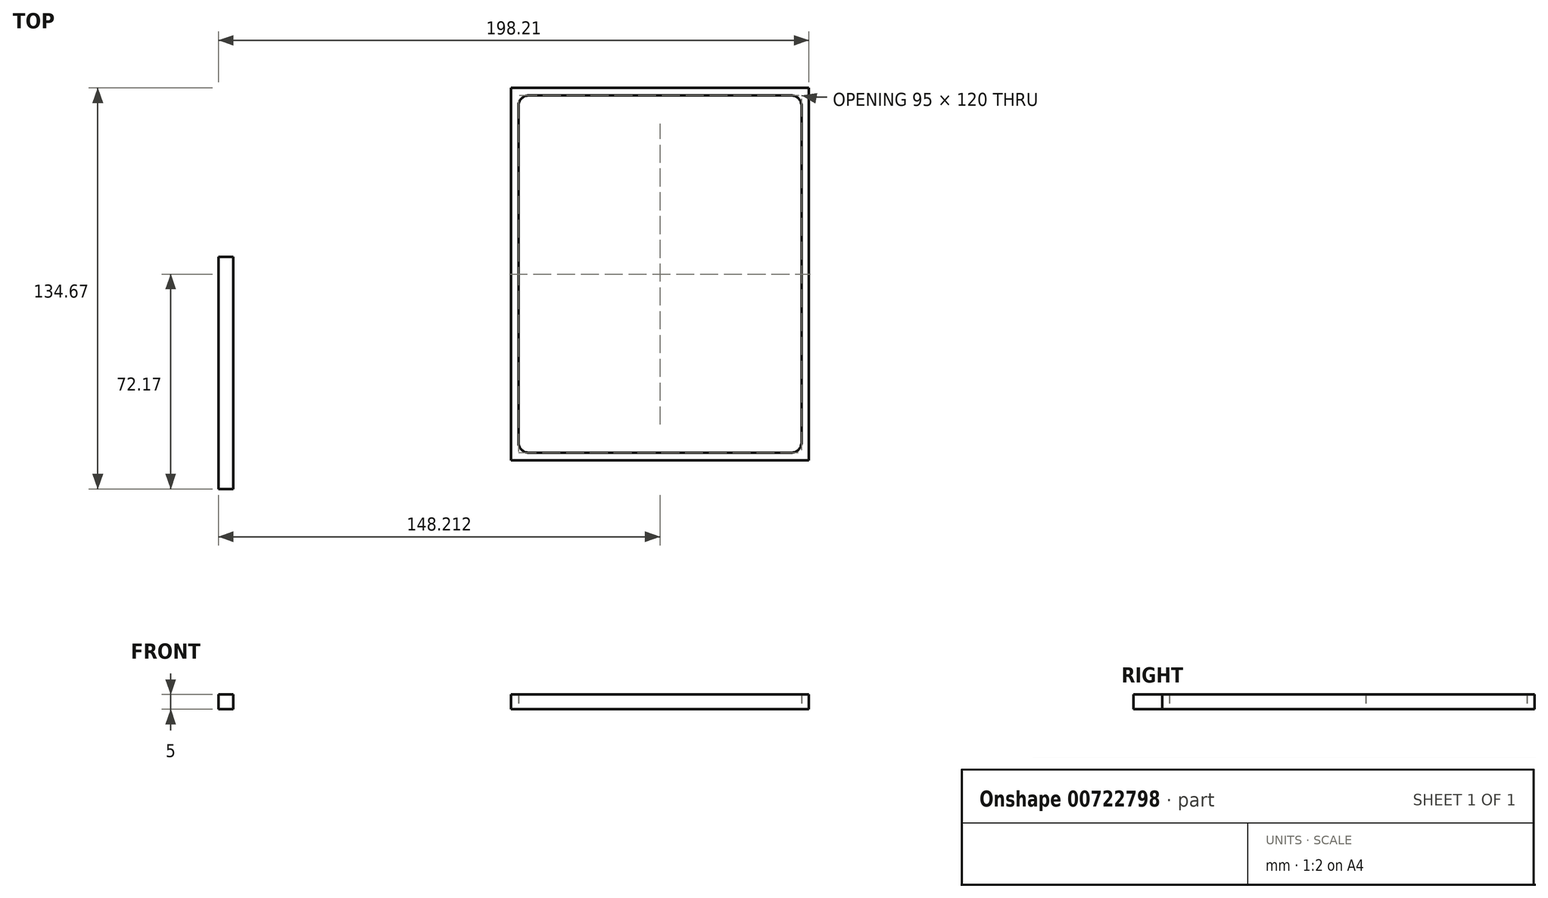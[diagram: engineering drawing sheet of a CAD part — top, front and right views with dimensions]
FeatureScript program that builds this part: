
annotation { "Feature Type Name" : "Feature", "Feature Type Description" : "" }
export const myFeature = defineFeature(function(context is Context, id is Id, definition is map)
    precondition{}
    {
        {
            var Q0;
            Q0=qCreatedBy(makeId("Top.planeOp"),FACE);
            var sketch = newSketch(context, id + "F0", { "sketchPlane" : qUnion([Q0])});
            skCircle(sketch, "E0", {"center": v(-29.27, 36.17) * mm, "radius": 8 * mm});
            skCircle(sketch, "E1", {"center": v(-29.27, 8.17) * mm, "radius": 8 * mm});
            skCircle(sketch, "E2", {"center": v(-29.27, -19.83) * mm, "radius": 8 * mm});
            skCircle(sketch, "E3", {"center": v(-29.27, -47.83) * mm, "radius": 8 * mm});
            skLineSegment(sketch, "E4.bottom", {"start": v(-47.27, 56.67) * mm, "end": v(52.73, 56.67) * mm});
            skLineSegment(sketch, "E4.top", {"start": v(-47.27, -68.33) * mm, "end": v(52.73, -68.33) * mm});
            skLineSegment(sketch, "E4.left", {"start": v(-47.27, 56.67) * mm, "end": v(-47.27, -68.33) * mm});
            skLineSegment(sketch, "E4.right", {"start": v(52.73, 56.67) * mm, "end": v(52.73, -68.33) * mm});
            skLineSegment(sketch, "E5", {"start": v(-11.8, -39.94) * mm, "end": v(-15.6, -39.94) * mm});
            skLineSegment(sketch, "E6", {"start": v(-15.6, -39.94) * mm, "end": v(-13.78, -36.83) * mm});
            skLineSegment(sketch, "E7", {"start": v(-13.78, -36.83) * mm, "end": v(-8.48, -36.83) * mm});
            skLineSegment(sketch, "E8", {"start": v(-8.48, -36.83) * mm, "end": v(-8.48, -58.83) * mm});
            skLineSegment(sketch, "E9", {"start": v(-11.8, -58.83) * mm, "end": v(-11.8, -39.94) * mm});
            skLineSegment(sketch, "E10", {"start": v(1.94, -39.94) * mm, "end": v(-1.87, -39.94) * mm});
            skLineSegment(sketch, "E11", {"start": v(-1.87, -39.94) * mm, "end": v(-0.04, -36.83) * mm});
            skLineSegment(sketch, "E12", {"start": v(-0.04, -36.83) * mm, "end": v(5.26, -36.83) * mm});
            skLineSegment(sketch, "E13", {"start": v(5.26, -36.83) * mm, "end": v(5.26, -58.83) * mm});
            skLineSegment(sketch, "E14", {"start": v(5.26, -58.83) * mm, "end": v(1.94, -58.83) * mm});
            skLineSegment(sketch, "E15", {"start": v(1.94, -58.83) * mm, "end": v(1.94, -39.94) * mm});
            skLineSegment(sketch, "E16", {"start": v(15.67, -39.94) * mm, "end": v(11.87, -39.94) * mm});
            skLineSegment(sketch, "E17", {"start": v(11.87, -39.94) * mm, "end": v(13.7, -36.83) * mm});
            skLineSegment(sketch, "E18", {"start": v(13.7, -36.83) * mm, "end": v(19, -36.83) * mm});
            skLineSegment(sketch, "E19", {"start": v(19, -36.83) * mm, "end": v(19, -58.83) * mm});
            skLineSegment(sketch, "E20", {"start": v(19, -58.83) * mm, "end": v(15.67, -58.83) * mm});
            skLineSegment(sketch, "E21", {"start": v(15.67, -58.83) * mm, "end": v(15.67, -39.94) * mm});
            skFitSpline(sketch, "E22", {"points": [v(28.68, -47.39) * mm, v(27.07, -46.25) * mm, v(26.26, -44.7) * mm, v(26.26, -42.73) * mm]});
            skFitSpline(sketch, "E23", {"points": [v(26.26, -42.73) * mm, v(26.26, -40.94) * mm, v(26.87, -39.45) * mm, v(28.1, -38.25) * mm]});
            skFitSpline(sketch, "E24", {"points": [v(28.1, -38.25) * mm, v(29.33, -37.06) * mm, v(30.87, -36.46) * mm, v(32.7, -36.46) * mm]});
            skFitSpline(sketch, "E25", {"points": [v(32.7, -36.46) * mm, v(34.52, -36.46) * mm, v(36.04, -37.06) * mm, v(37.26, -38.25) * mm]});
            skFitSpline(sketch, "E26", {"points": [v(37.26, -38.25) * mm, v(38.47, -39.44) * mm, v(39.08, -40.94) * mm, v(39.08, -42.74) * mm]});
            skFitSpline(sketch, "E27", {"points": [v(39.08, -42.74) * mm, v(39.08, -44.63) * mm, v(38.28, -46.18) * mm, v(36.67, -47.37) * mm]});
            skFitSpline(sketch, "E28", {"points": [v(36.67, -47.37) * mm, v(37.56, -47.85) * mm, v(38.25, -48.54) * mm, v(38.75, -49.45) * mm]});
            skFitSpline(sketch, "E29", {"points": [v(38.75, -49.45) * mm, v(39.27, -50.37) * mm, v(39.52, -51.4) * mm, v(39.52, -52.53) * mm]});
            skFitSpline(sketch, "E30", {"points": [v(39.52, -52.53) * mm, v(39.52, -54.48) * mm, v(38.89, -56.07) * mm, v(37.61, -57.32) * mm]});
            skFitSpline(sketch, "E31", {"points": [v(37.61, -57.32) * mm, v(36.34, -58.56) * mm, v(34.71, -59.19) * mm, v(32.73, -59.19) * mm]});
            skFitSpline(sketch, "E32", {"points": [v(32.73, -59.19) * mm, v(30.7, -59.19) * mm, v(29.02, -58.56) * mm, v(27.7, -57.3) * mm]});
            skFitSpline(sketch, "E33", {"points": [v(27.7, -57.3) * mm, v(26.37, -56.05) * mm, v(25.7, -54.47) * mm, v(25.7, -52.57) * mm]});
            skFitSpline(sketch, "E34", {"points": [v(25.7, -52.57) * mm, v(25.7, -50.1) * mm, v(26.7, -48.38) * mm, v(28.68, -47.39) * mm]});
            skFitSpline(sketch, "E35", {"points": [v(29.38, -42.71) * mm, v(29.38, -43.65) * mm, v(29.7, -44.44) * mm, v(30.33, -45.08) * mm]});
            skFitSpline(sketch, "E36", {"points": [v(30.33, -45.08) * mm, v(30.98, -45.73) * mm, v(31.76, -46.05) * mm, v(32.67, -46.05) * mm]});
            skFitSpline(sketch, "E37", {"points": [v(32.67, -46.05) * mm, v(33.57, -46.05) * mm, v(34.35, -45.73) * mm, v(35, -45.08) * mm]});
            skFitSpline(sketch, "E38", {"points": [v(35, -45.08) * mm, v(35.64, -44.43) * mm, v(35.96, -43.66) * mm, v(35.96, -42.76) * mm]});
            skFitSpline(sketch, "E39", {"points": [v(35.96, -42.76) * mm, v(35.96, -41.85) * mm, v(35.64, -41.08) * mm, v(35, -40.43) * mm]});
            skFitSpline(sketch, "E40", {"points": [v(35, -40.43) * mm, v(34.35, -39.79) * mm, v(33.57, -39.47) * mm, v(32.67, -39.47) * mm]});
            skFitSpline(sketch, "E41", {"points": [v(32.67, -39.47) * mm, v(31.77, -39.47) * mm, v(31, -39.79) * mm, v(30.35, -40.43) * mm]});
            skFitSpline(sketch, "E42", {"points": [v(30.35, -40.43) * mm, v(29.7, -41.08) * mm, v(29.38, -41.84) * mm, v(29.38, -42.71) * mm]});
            skFitSpline(sketch, "E43", {"points": [v(28.97, -52.46) * mm, v(28.97, -53.48) * mm, v(29.32, -54.35) * mm, v(30.02, -55.08) * mm]});
            skFitSpline(sketch, "E44", {"points": [v(30.02, -55.08) * mm, v(30.73, -55.8) * mm, v(31.6, -56.17) * mm, v(32.61, -56.17) * mm]});
            skFitSpline(sketch, "E45", {"points": [v(32.61, -56.17) * mm, v(33.62, -56.17) * mm, v(34.48, -55.8) * mm, v(35.2, -55.1) * mm]});
            skFitSpline(sketch, "E46", {"points": [v(35.2, -55.1) * mm, v(35.9, -54.37) * mm, v(36.26, -53.51) * mm, v(36.26, -52.5) * mm]});
            skFitSpline(sketch, "E47", {"points": [v(36.26, -52.5) * mm, v(36.26, -51.49) * mm, v(35.9, -50.62) * mm, v(35.2, -49.91) * mm]});
            skFitSpline(sketch, "E48", {"points": [v(35.2, -49.91) * mm, v(34.48, -49.2) * mm, v(33.62, -48.84) * mm, v(32.61, -48.84) * mm]});
            skFitSpline(sketch, "E49", {"points": [v(32.61, -48.84) * mm, v(31.62, -48.84) * mm, v(30.76, -49.2) * mm, v(30.03, -49.91) * mm]});
            skFitSpline(sketch, "E50", {"points": [v(30.03, -49.91) * mm, v(29.32, -50.62) * mm, v(28.97, -51.47) * mm, v(28.97, -52.46) * mm]});
            skLineSegment(sketch, "E51", {"start": v(-11.8, -11.94) * mm, "end": v(-15.6, -11.94) * mm});
            skLineSegment(sketch, "E52", {"start": v(-15.6, -11.94) * mm, "end": v(-13.78, -8.83) * mm});
            skLineSegment(sketch, "E53", {"start": v(-13.78, -8.83) * mm, "end": v(-8.48, -8.83) * mm});
            skLineSegment(sketch, "E54", {"start": v(-8.48, -8.83) * mm, "end": v(-8.48, -30.83) * mm});
            skLineSegment(sketch, "E55", {"start": v(-8.48, -30.83) * mm, "end": v(-11.8, -30.83) * mm});
            skLineSegment(sketch, "E56", {"start": v(-11.8, -30.83) * mm, "end": v(-11.8, -11.94) * mm});
            skLineSegment(sketch, "E57", {"start": v(1.94, -11.94) * mm, "end": v(-1.87, -11.94) * mm});
            skLineSegment(sketch, "E58", {"start": v(-1.87, -11.94) * mm, "end": v(-0.04, -8.83) * mm});
            skLineSegment(sketch, "E59", {"start": v(-0.04, -8.83) * mm, "end": v(5.26, -8.83) * mm});
            skLineSegment(sketch, "E60", {"start": v(5.26, -8.83) * mm, "end": v(5.26, -30.83) * mm});
            skLineSegment(sketch, "E61", {"start": v(5.26, -30.83) * mm, "end": v(1.94, -30.83) * mm});
            skLineSegment(sketch, "E62", {"start": v(1.94, -30.83) * mm, "end": v(1.94, -11.94) * mm});
            skLineSegment(sketch, "E63", {"start": v(17.07, -27.7) * mm, "end": v(25.26, -27.7) * mm});
            skLineSegment(sketch, "E64", {"start": v(25.26, -27.7) * mm, "end": v(25.26, -30.83) * mm});
            skLineSegment(sketch, "E65", {"start": v(25.26, -30.83) * mm, "end": v(10.49, -30.83) * mm});
            skLineSegment(sketch, "E66", {"start": v(10.49, -30.83) * mm, "end": v(18.12, -21.58) * mm});
            skFitSpline(sketch, "E67", {"points": [v(18.12, -21.58) * mm, v(18.87, -20.66) * mm, v(19.5, -19.86) * mm, v(20, -19.19) * mm]});
            skFitSpline(sketch, "E68", {"points": [v(20, -19.19) * mm, v(20.52, -18.51) * mm, v(20.9, -17.95) * mm, v(21.17, -17.5) * mm]});
            skFitSpline(sketch, "E69", {"points": [v(21.17, -17.5) * mm, v(21.71, -16.6) * mm, v(21.99, -15.8) * mm, v(21.99, -15.08) * mm]});
            skFitSpline(sketch, "E70", {"points": [v(21.99, -15.08) * mm, v(21.99, -14.06) * mm, v(21.62, -13.2) * mm, v(20.9, -12.5) * mm]});
            skFitSpline(sketch, "E71", {"points": [v(20.9, -12.5) * mm, v(20.18, -11.81) * mm, v(19.29, -11.47) * mm, v(18.22, -11.47) * mm]});
            skFitSpline(sketch, "E72", {"points": [v(18.22, -11.47) * mm, v(16, -11.47) * mm, v(14.73, -12.78) * mm, v(14.4, -15.41) * mm]});
            skLineSegment(sketch, "E73", {"start": v(14.4, -15.41) * mm, "end": v(11.1, -15.41) * mm});
            skFitSpline(sketch, "E74", {"points": [v(11.1, -15.41) * mm, v(11.63, -10.78) * mm, v(13.97, -8.46) * mm, v(18.12, -8.46) * mm]});
            skFitSpline(sketch, "E75", {"points": [v(18.12, -8.46) * mm, v(20.13, -8.46) * mm, v(21.8, -9.1) * mm, v(23.17, -10.37) * mm]});
            skFitSpline(sketch, "E76", {"points": [v(23.17, -10.37) * mm, v(24.54, -11.64) * mm, v(25.22, -13.22) * mm, v(25.22, -15.1) * mm]});
            skFitSpline(sketch, "E77", {"points": [v(25.22, -15.1) * mm, v(25.22, -16.3) * mm, v(24.9, -17.47) * mm, v(24.26, -18.62) * mm]});
            skFitSpline(sketch, "E78", {"points": [v(24.26, -18.62) * mm, v(23.94, -19.22) * mm, v(23.47, -19.93) * mm, v(22.84, -20.76) * mm]});
            skFitSpline(sketch, "E79", {"points": [v(22.84, -20.76) * mm, v(22.22, -21.57) * mm, v(21.44, -22.54) * mm, v(20.49, -23.66) * mm]});
            skLineSegment(sketch, "E80", {"start": v(20.49, -23.66) * mm, "end": v(17.07, -27.7) * mm});
            skFitSpline(sketch, "E81", {"points": [v(29, -19.69) * mm, v(29, -16.18) * mm, v(29.83, -13.38) * mm, v(31.46, -11.3) * mm]});
            skFitSpline(sketch, "E82", {"points": [v(31.46, -11.3) * mm, v(32.92, -9.4) * mm, v(34.7, -8.46) * mm, v(36.78, -8.46) * mm]});
            skFitSpline(sketch, "E83", {"points": [v(36.78, -8.46) * mm, v(38.86, -8.46) * mm, v(40.63, -9.4) * mm, v(42.09, -11.3) * mm]});
            skFitSpline(sketch, "E84", {"points": [v(42.09, -11.3) * mm, v(43.72, -13.38) * mm, v(44.54, -16.23) * mm, v(44.54, -19.83) * mm]});
            skFitSpline(sketch, "E85", {"points": [v(44.54, -19.83) * mm, v(44.54, -23.42) * mm, v(43.72, -26.26) * mm, v(42.09, -28.35) * mm]});
            skFitSpline(sketch, "E86", {"points": [v(42.09, -28.35) * mm, v(40.63, -30.24) * mm, v(38.86, -31.19) * mm, v(36.79, -31.19) * mm]});
            skFitSpline(sketch, "E87", {"points": [v(36.79, -31.19) * mm, v(34.72, -31.19) * mm, v(32.94, -30.24) * mm, v(31.46, -28.35) * mm]});
            skFitSpline(sketch, "E88", {"points": [v(31.46, -28.35) * mm, v(29.83, -26.26) * mm, v(29, -23.37) * mm, v(29, -19.69) * mm]});
            skFitSpline(sketch, "E89", {"points": [v(32.27, -19.7) * mm, v(32.27, -22.14) * mm, v(32.7, -24.17) * mm, v(33.54, -25.79) * mm]});
            skFitSpline(sketch, "E90", {"points": [v(33.54, -25.79) * mm, v(34.39, -27.37) * mm, v(35.46, -28.17) * mm, v(36.78, -28.17) * mm]});
            skFitSpline(sketch, "E91", {"points": [v(36.78, -28.17) * mm, v(38.08, -28.17) * mm, v(39.15, -27.37) * mm, v(40, -25.79) * mm]});
            skFitSpline(sketch, "E92", {"points": [v(40, -25.79) * mm, v(40.86, -24.2) * mm, v(41.3, -22.22) * mm, v(41.3, -19.82) * mm]});
            skFitSpline(sketch, "E93", {"points": [v(41.3, -19.82) * mm, v(41.3, -17.41) * mm, v(40.86, -15.42) * mm, v(40, -13.83) * mm]});
            skFitSpline(sketch, "E94", {"points": [v(40, -13.83) * mm, v(39.15, -12.25) * mm, v(38.08, -11.47) * mm, v(36.78, -11.47) * mm]});
            skFitSpline(sketch, "E95", {"points": [v(36.78, -11.47) * mm, v(35.48, -11.47) * mm, v(34.4, -12.25) * mm, v(33.55, -13.83) * mm]});
            skFitSpline(sketch, "E96", {"points": [v(33.55, -13.83) * mm, v(32.7, -15.4) * mm, v(32.27, -17.36) * mm, v(32.27, -19.7) * mm]});
            skLineSegment(sketch, "E97", {"start": v(-11.86, 16.06) * mm, "end": v(-15.66, 16.06) * mm});
            skLineSegment(sketch, "E98", {"start": v(-15.66, 16.06) * mm, "end": v(-13.84, 19.17) * mm});
            skLineSegment(sketch, "E99", {"start": v(-13.84, 19.17) * mm, "end": v(-8.54, 19.17) * mm});
            skLineSegment(sketch, "E100", {"start": v(-8.54, 19.17) * mm, "end": v(-8.54, -2.83) * mm});
            skLineSegment(sketch, "E101", {"start": v(-8.54, -2.83) * mm, "end": v(-11.86, -2.83) * mm});
            skLineSegment(sketch, "E102", {"start": v(-11.86, -2.83) * mm, "end": v(-11.86, 16.06) * mm});
            skLineSegment(sketch, "E103", {"start": v(1.88, 16.06) * mm, "end": v(-1.93, 16.06) * mm});
            skLineSegment(sketch, "E104", {"start": v(-1.93, 16.06) * mm, "end": v(-0.1, 19.17) * mm});
            skLineSegment(sketch, "E105", {"start": v(-0.1, 19.17) * mm, "end": v(5.2, 19.17) * mm});
            skLineSegment(sketch, "E106", {"start": v(5.2, 19.17) * mm, "end": v(5.2, -2.83) * mm});
            skLineSegment(sketch, "E107", {"start": v(5.2, -2.83) * mm, "end": v(1.88, -2.83) * mm});
            skLineSegment(sketch, "E108", {"start": v(1.88, -2.83) * mm, "end": v(1.88, 16.06) * mm});
            skLineSegment(sketch, "E109", {"start": v(17, 0.3) * mm, "end": v(25.2, 0.3) * mm});
            skLineSegment(sketch, "E110", {"start": v(25.2, 0.3) * mm, "end": v(25.2, -2.83) * mm});
            skLineSegment(sketch, "E111", {"start": v(25.2, -2.83) * mm, "end": v(10.42, -2.83) * mm});
            skLineSegment(sketch, "E112", {"start": v(10.42, -2.83) * mm, "end": v(18.06, 6.42) * mm});
            skFitSpline(sketch, "E113", {"points": [v(18.06, 6.42) * mm, v(18.81, 7.34) * mm, v(19.44, 8.14) * mm, v(19.94, 8.81) * mm]});
            skFitSpline(sketch, "E114", {"points": [v(19.94, 8.81) * mm, v(20.46, 9.49) * mm, v(20.85, 10.05) * mm, v(21.11, 10.5) * mm]});
            skFitSpline(sketch, "E115", {"points": [v(21.11, 10.5) * mm, v(21.65, 11.4) * mm, v(21.92, 12.2) * mm, v(21.92, 12.92) * mm]});
            skFitSpline(sketch, "E116", {"points": [v(21.92, 12.92) * mm, v(21.92, 13.94) * mm, v(21.56, 14.8) * mm, v(20.84, 15.5) * mm]});
            skFitSpline(sketch, "E117", {"points": [v(20.84, 15.5) * mm, v(20.12, 16.19) * mm, v(19.23, 16.53) * mm, v(18.16, 16.53) * mm]});
            skFitSpline(sketch, "E118", {"points": [v(18.16, 16.53) * mm, v(15.94, 16.53) * mm, v(14.67, 15.22) * mm, v(14.34, 12.59) * mm]});
            skLineSegment(sketch, "E119", {"start": v(14.34, 12.59) * mm, "end": v(11.04, 12.59) * mm});
            skFitSpline(sketch, "E120", {"points": [v(11.04, 12.59) * mm, v(11.57, 17.22) * mm, v(13.91, 19.54) * mm, v(18.06, 19.54) * mm]});
            skFitSpline(sketch, "E121", {"points": [v(18.06, 19.54) * mm, v(20.07, 19.54) * mm, v(21.75, 18.9) * mm, v(23.1, 17.63) * mm]});
            skFitSpline(sketch, "E122", {"points": [v(23.1, 17.63) * mm, v(24.47, 16.36) * mm, v(25.16, 14.78) * mm, v(25.16, 12.9) * mm]});
            skFitSpline(sketch, "E123", {"points": [v(25.16, 12.9) * mm, v(25.16, 11.7) * mm, v(24.84, 10.53) * mm, v(24.2, 9.38) * mm]});
            skFitSpline(sketch, "E124", {"points": [v(24.2, 9.38) * mm, v(23.88, 8.78) * mm, v(23.4, 8.07) * mm, v(22.78, 7.24) * mm]});
            skFitSpline(sketch, "E125", {"points": [v(22.78, 7.24) * mm, v(22.16, 6.43) * mm, v(21.38, 5.46) * mm, v(20.43, 4.34) * mm]});
            skLineSegment(sketch, "E126", {"start": v(20.43, 4.34) * mm, "end": v(17, 0.3) * mm});
            skLineSegment(sketch, "E127", {"start": v(35.02, 0.3) * mm, "end": v(43.21, 0.3) * mm});
            skLineSegment(sketch, "E128", {"start": v(43.21, 0.3) * mm, "end": v(43.21, -2.83) * mm});
            skLineSegment(sketch, "E129", {"start": v(43.21, -2.83) * mm, "end": v(28.44, -2.83) * mm});
            skLineSegment(sketch, "E130", {"start": v(28.44, -2.83) * mm, "end": v(36.07, 6.42) * mm});
            skFitSpline(sketch, "E131", {"points": [v(36.07, 6.42) * mm, v(36.82, 7.34) * mm, v(37.45, 8.14) * mm, v(37.95, 8.81) * mm]});
            skFitSpline(sketch, "E132", {"points": [v(37.95, 8.81) * mm, v(38.47, 9.49) * mm, v(38.86, 10.05) * mm, v(39.12, 10.5) * mm]});
            skFitSpline(sketch, "E133", {"points": [v(39.12, 10.5) * mm, v(39.66, 11.4) * mm, v(39.93, 12.2) * mm, v(39.93, 12.92) * mm]});
            skFitSpline(sketch, "E134", {"points": [v(39.93, 12.92) * mm, v(39.93, 13.94) * mm, v(39.57, 14.8) * mm, v(38.85, 15.5) * mm]});
            skFitSpline(sketch, "E135", {"points": [v(38.85, 15.5) * mm, v(38.13, 16.19) * mm, v(37.24, 16.53) * mm, v(36.17, 16.53) * mm]});
            skFitSpline(sketch, "E136", {"points": [v(36.17, 16.53) * mm, v(33.95, 16.53) * mm, v(32.68, 15.22) * mm, v(32.35, 12.59) * mm]});
            skLineSegment(sketch, "E137", {"start": v(32.35, 12.59) * mm, "end": v(29.05, 12.59) * mm});
            skFitSpline(sketch, "E138", {"points": [v(29.05, 12.59) * mm, v(29.58, 17.22) * mm, v(31.92, 19.54) * mm, v(36.07, 19.54) * mm]});
            skFitSpline(sketch, "E139", {"points": [v(36.07, 19.54) * mm, v(38.08, 19.54) * mm, v(39.76, 18.9) * mm, v(41.12, 17.63) * mm]});
            skFitSpline(sketch, "E140", {"points": [v(41.12, 17.63) * mm, v(42.48, 16.36) * mm, v(43.17, 14.78) * mm, v(43.17, 12.9) * mm]});
            skFitSpline(sketch, "E141", {"points": [v(43.17, 12.9) * mm, v(43.17, 11.7) * mm, v(42.85, 10.53) * mm, v(42.21, 9.38) * mm]});
            skFitSpline(sketch, "E142", {"points": [v(42.21, 9.38) * mm, v(41.9, 8.78) * mm, v(41.42, 8.07) * mm, v(40.79, 7.24) * mm]});
            skFitSpline(sketch, "E143", {"points": [v(40.79, 7.24) * mm, v(40.17, 6.43) * mm, v(39.39, 5.46) * mm, v(38.44, 4.34) * mm]});
            skLineSegment(sketch, "E144", {"start": v(38.44, 4.34) * mm, "end": v(35.02, 0.3) * mm});
            skLineSegment(sketch, "E145", {"start": v(-11.74, 44.06) * mm, "end": v(-15.55, 44.06) * mm});
            skLineSegment(sketch, "E146", {"start": v(-15.55, 44.06) * mm, "end": v(-13.72, 47.17) * mm});
            skLineSegment(sketch, "E147", {"start": v(-13.72, 47.17) * mm, "end": v(-8.42, 47.17) * mm});
            skLineSegment(sketch, "E148", {"start": v(-8.42, 47.17) * mm, "end": v(-8.42, 25.17) * mm});
            skLineSegment(sketch, "E149", {"start": v(-8.42, 25.17) * mm, "end": v(-11.74, 25.17) * mm});
            skLineSegment(sketch, "E150", {"start": v(-11.74, 25.17) * mm, "end": v(-11.74, 44.06) * mm});
            skLineSegment(sketch, "E151", {"start": v(2, 44.06) * mm, "end": v(-1.8, 44.06) * mm});
            skLineSegment(sketch, "E152", {"start": v(-1.8, 44.06) * mm, "end": v(0.01, 47.17) * mm});
            skLineSegment(sketch, "E153", {"start": v(0.01, 47.17) * mm, "end": v(5.31, 47.17) * mm});
            skLineSegment(sketch, "E154", {"start": v(5.31, 47.17) * mm, "end": v(5.31, 25.17) * mm});
            skLineSegment(sketch, "E155", {"start": v(5.31, 25.17) * mm, "end": v(2, 25.17) * mm});
            skLineSegment(sketch, "E156", {"start": v(2, 25.17) * mm, "end": v(2, 44.06) * mm});
            skLineSegment(sketch, "E157", {"start": v(17.13, 28.3) * mm, "end": v(25.32, 28.3) * mm});
            skLineSegment(sketch, "E158", {"start": v(25.32, 28.3) * mm, "end": v(25.32, 25.17) * mm});
            skLineSegment(sketch, "E159", {"start": v(25.32, 25.17) * mm, "end": v(10.54, 25.17) * mm});
            skLineSegment(sketch, "E160", {"start": v(10.54, 25.17) * mm, "end": v(18.18, 34.42) * mm});
            skFitSpline(sketch, "E161", {"points": [v(18.18, 34.42) * mm, v(18.93, 35.34) * mm, v(19.56, 36.14) * mm, v(20.06, 36.81) * mm]});
            skFitSpline(sketch, "E162", {"points": [v(20.06, 36.81) * mm, v(20.58, 37.49) * mm, v(20.96, 38.05) * mm, v(21.23, 38.5) * mm]});
            skFitSpline(sketch, "E163", {"points": [v(21.23, 38.5) * mm, v(21.77, 39.4) * mm, v(22.04, 40.2) * mm, v(22.04, 40.92) * mm]});
            skFitSpline(sketch, "E164", {"points": [v(22.04, 40.92) * mm, v(22.04, 41.94) * mm, v(21.68, 42.8) * mm, v(20.96, 43.5) * mm]});
            skFitSpline(sketch, "E165", {"points": [v(20.96, 43.5) * mm, v(20.24, 44.19) * mm, v(19.35, 44.53) * mm, v(18.28, 44.53) * mm]});
            skFitSpline(sketch, "E166", {"points": [v(18.28, 44.53) * mm, v(16.06, 44.53) * mm, v(14.79, 43.22) * mm, v(14.46, 40.59) * mm]});
            skLineSegment(sketch, "E167", {"start": v(14.46, 40.59) * mm, "end": v(11.16, 40.59) * mm});
            skFitSpline(sketch, "E168", {"points": [v(11.16, 40.59) * mm, v(11.69, 45.22) * mm, v(14.03, 47.54) * mm, v(18.18, 47.54) * mm]});
            skFitSpline(sketch, "E169", {"points": [v(18.18, 47.54) * mm, v(20.19, 47.54) * mm, v(21.87, 46.9) * mm, v(23.23, 45.63) * mm]});
            skFitSpline(sketch, "E170", {"points": [v(23.23, 45.63) * mm, v(24.6, 44.36) * mm, v(25.28, 42.78) * mm, v(25.28, 40.9) * mm]});
            skFitSpline(sketch, "E171", {"points": [v(25.28, 40.9) * mm, v(25.28, 39.7) * mm, v(24.96, 38.53) * mm, v(24.32, 37.38) * mm]});
            skFitSpline(sketch, "E172", {"points": [v(24.32, 37.38) * mm, v(24, 36.78) * mm, v(23.52, 36.07) * mm, v(22.9, 35.24) * mm]});
            skFitSpline(sketch, "E173", {"points": [v(22.9, 35.24) * mm, v(22.28, 34.43) * mm, v(21.5, 33.46) * mm, v(20.55, 32.34) * mm]});
            skLineSegment(sketch, "E174", {"start": v(20.55, 32.34) * mm, "end": v(17.13, 28.3) * mm});
            skLineSegment(sketch, "E175", {"start": v(42.05, 31.31) * mm, "end": v(44.38, 31.31) * mm});
            skLineSegment(sketch, "E176", {"start": v(44.38, 31.31) * mm, "end": v(44.38, 28.3) * mm});
            skLineSegment(sketch, "E177", {"start": v(44.38, 28.3) * mm, "end": v(42.05, 28.3) * mm});
            skLineSegment(sketch, "E178", {"start": v(42.05, 28.3) * mm, "end": v(42.05, 25.17) * mm});
            skLineSegment(sketch, "E179", {"start": v(42.05, 25.17) * mm, "end": v(38.73, 25.17) * mm});
            skLineSegment(sketch, "E180", {"start": v(38.73, 25.17) * mm, "end": v(38.73, 28.3) * mm});
            skLineSegment(sketch, "E181", {"start": v(38.73, 28.3) * mm, "end": v(27.93, 28.3) * mm});
            skLineSegment(sketch, "E182", {"start": v(27.93, 28.3) * mm, "end": v(42.05, 48.8) * mm});
            skLineSegment(sketch, "E183", {"start": v(42.05, 48.8) * mm, "end": v(42.05, 43.5) * mm});
            skLineSegment(sketch, "E184", {"start": v(38.73, 31.31) * mm, "end": v(38.73, 35) * mm});
            skLineSegment(sketch, "E185", {"start": v(38.73, 38.68) * mm, "end": v(33.66, 31.31) * mm});
            skLineSegment(sketch, "E186", {"start": v(33.66, 31.31) * mm, "end": v(38.73, 31.31) * mm});
            skCircle(sketch, "E187", {"center": v(-41.27, 50.67) * mm, "radius": 1.75 * mm});
            skCircle(sketch, "E188", {"center": v(46.73, 50.67) * mm, "radius": 1.75 * mm});
            skCircle(sketch, "E189", {"center": v(-41.27, -62.33) * mm, "radius": 1.75 * mm});
            skCircle(sketch, "E190", {"center": v(46.73, -62.33) * mm, "radius": 1.75 * mm});
            skLineSegment(sketch, "E191", {"start": v(33.66, 31.31) * mm, "end": v(42.05, 43.5) * mm});
            skLineSegment(sketch, "E192", {"start": v(38.73, 35) * mm, "end": v(42.05, 35) * mm});
            skLineSegment(sketch, "E193.trimOffspring", {"start": v(42.05, 35) * mm, "end": v(42.05, 31.31) * mm});
            skPoint(sketch, "E194.orphan", {"position": v(38.73, 38.68) * mm});
            skLineSegment(sketch, "E195.left", {"start": v(36.03, -8.5) * mm, "end": v(36.03, -11.56) * mm});
            skLineSegment(sketch, "E195.right", {"start": v(37.54, -8.5) * mm, "end": v(37.54, -11.56) * mm});
            skLineSegment(sketch, "E196.trimOffspring", {"start": v(36.03, -28.07) * mm, "end": v(36.03, -31.14) * mm});
            skLineSegment(sketch, "E197.trimOffspring", {"start": v(37.54, -28.07) * mm, "end": v(37.54, -31.14) * mm});
            skLineSegment(sketch, "E198.left", {"start": v(31.91, -36.5) * mm, "end": v(31.91, -39.55) * mm});
            skLineSegment(sketch, "E198.right", {"start": v(33.43, -36.5) * mm, "end": v(33.43, -39.55) * mm});
            skLineSegment(sketch, "E199.trimOffspring", {"start": v(33.43, -56.08) * mm, "end": v(33.43, -59.16) * mm});
            skLineSegment(sketch, "E200.trimOffspring", {"start": v(31.91, -56.1) * mm, "end": v(31.91, -59.15) * mm});
            skLineSegment(sketch, "E201.trimOffspring", {"start": v(33.43, -45.97) * mm, "end": v(33.43, -48.93) * mm});
            skLineSegment(sketch, "E202.trimOffspring", {"start": v(31.91, -45.97) * mm, "end": v(31.91, -48.9) * mm});
            skLineSegment(sketch, "E203", {"start": v(-11.8, -58.83) * mm, "end": v(-8.48, -58.83) * mm});
            skCircle(sketch, "E204", {"center": v(-41.27, 50.67) * mm, "radius": 3.5 * mm});
            skCircle(sketch, "E205", {"center": v(46.73, 50.67) * mm, "radius": 3.5 * mm});
            skCircle(sketch, "E206", {"center": v(-41.27, -62.33) * mm, "radius": 3.5 * mm});
            skCircle(sketch, "E207", {"center": v(46.73, -62.33) * mm, "radius": 3.5 * mm});
            skLineSegment(sketch, "E208", {"start": v(50.23, -62.33) * mm, "end": v(50.23, 50.67) * mm});
            skLineSegment(sketch, "E209", {"start": v(-44.77, 50.67) * mm, "end": v(-44.77, -62.33) * mm});
            skLineSegment(sketch, "E210", {"start": v(-41.27, -65.83) * mm, "end": v(46.73, -65.83) * mm});
            skLineSegment(sketch, "E211", {"start": v(-38.1, -63.83) * mm, "end": v(43.57, -63.83) * mm});
            skLineSegment(sketch, "E212", {"start": v(46.73, -58.83) * mm, "end": v(46.73, 47.17) * mm});
            skLineSegment(sketch, "E213", {"start": v(-41.27, 47.17) * mm, "end": v(-41.27, -58.83) * mm});
            skLineSegment(sketch, "E214.bottom", {"start": v(-145.48, 0) * mm, "end": v(-140.48, 0) * mm});
            skLineSegment(sketch, "E214.top", {"start": v(-145.48, -78) * mm, "end": v(-140.48, -78) * mm});
            skLineSegment(sketch, "E214.left", {"start": v(-145.48, 0) * mm, "end": v(-145.48, -78) * mm});
            skLineSegment(sketch, "E214.right", {"start": v(-140.48, 0) * mm, "end": v(-140.48, -78) * mm});
            skPoint(sketch, "E215.start.orphan", {"position": v(43.23, 50.67) * mm});
            skLineSegment(sketch, "E216", {"start": v(-41.27, 54.17) * mm, "end": v(46.73, 54.17) * mm});
            skLineSegment(sketch, "E217", {"start": v(-38.1, 52.17) * mm, "end": v(43.57, 52.17) * mm});
            skSolve(sketch);
        }
        {
            var Q0;
            Q0 = qSketchRegion(id + "F0", true);
            extrude(context, id + "F1", {"entities" : qUnion([Q0]), "depth" : 5 * mm, "offsetDistance" : 25 * mm});
        }
    });
